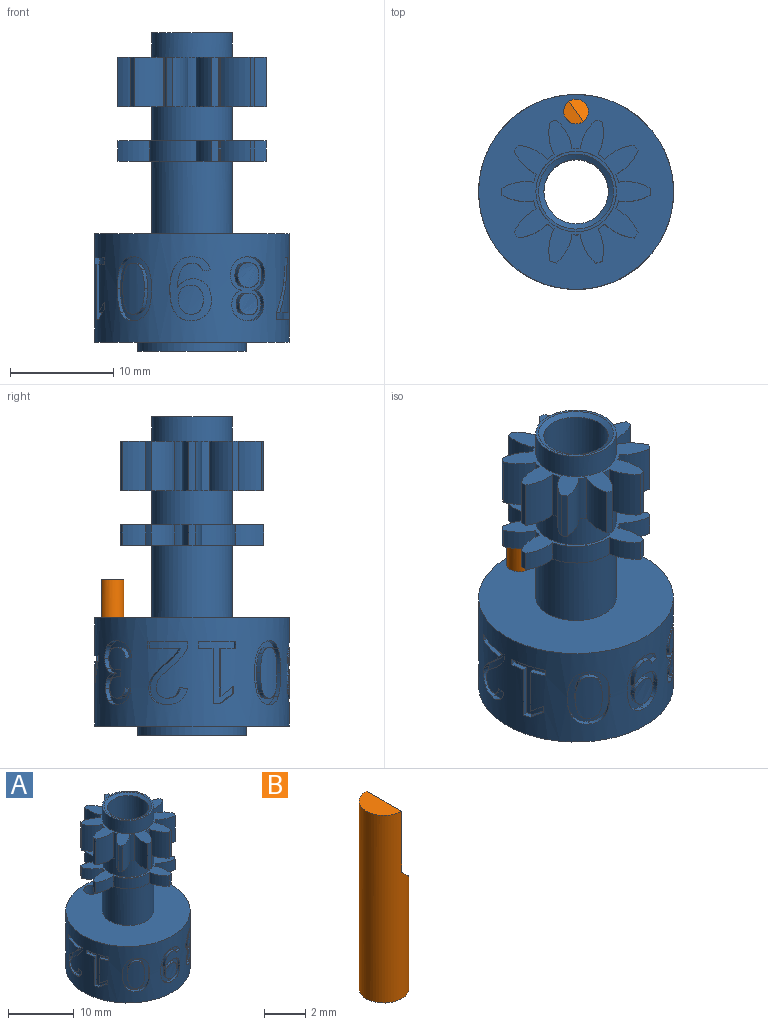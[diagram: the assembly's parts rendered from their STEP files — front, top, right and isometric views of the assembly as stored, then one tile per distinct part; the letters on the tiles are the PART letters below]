
ASSEMBLY  parts=2 mates=1
PART A: 322 faces, bbox 19.1x19x30.9 mm
  f0: cylinder r=9.45mm len=18.9mm, axis (0,0,-1), area 491.1mm2, adj f6,f7,f91,f92,f93,f94,f95,f102
  f1: cylinder r=3.9mm len=7.8mm, axis (0,0,-1), area 58.8mm2, adj f9,f87
  f2: cylinder r=3.9mm len=7.8mm, axis (0,0,-1), area 80.9mm2, adj f13,f88
  f3: cone r=3.12mm half-angle=30deg, axis (0,0,-1), area 49.7mm2, adj f4,f10
  f4: plane 10.5x10.5mm, normal (0,0,-1), area 31.2mm2, adj f3,f5
  f5: cylinder r=5.25mm len=10.5mm, axis (0,0,-1), area 29.7mm2, adj f4,f6
  f6: plane 18.9x18.9mm, normal (0,0,-1), area 189.4mm2, adj f0,f5,f11
  f7: plane 18.9x18.9mm, normal (0,0,1), area 228.2mm2, adj f0,f8,f11
  f8: cylinder r=3.9mm len=7.8mm, axis (0,0,-1), area 172.8mm2, adj f7,f14
  f9: plane 7.8x7.8mm, normal (0,0,1), area 6.2mm2, adj f1,f12
  f10: cylinder r=3.12mm len=28.73mm, axis (0,0,-1), area 563.2mm2, adj f3,f12
  f11: cylinder r=1.2mm len=10.5mm, axis (0,0,1), area 77.2mm2, adj f6,f7,f89,f90,f91,f92,f93,f94
  f12: cone r=3.64mm half-angle=60deg, axis (0,0,1), area 12.7mm2, adj f9,f10
  f13: plane 14.4x13.88mm, normal (0,0,1), area 46.7mm2, adj f2,f15,f16,f17,f18,f19,f20,f21
  f14: plane 14.4x13.88mm, normal (0,0,-1), area 46.7mm2, adj f8,f15,f16,f17,f18,f19,f20,f21
  f15: cylinder r=4.2mm len=1.95mm, axis (0,0,-1), area 1.6mm2, adj f13,f14,f16,f17
  f16: cylinder r=4.5mm len=2.3mm, axis (0,0,-1), area 6.3mm2, adj f13,f14,f15,f21
  f17: cylinder r=4.5mm len=3.09mm, axis (0,0,-1), area 6.3mm2, adj f13,f14,f15,f46
  f18: cylinder r=4.5mm len=2.85mm, axis (0,0,-1), area 6.3mm2, adj f13,f14,f19,f21
  f19: cylinder r=4.2mm len=1.95mm, axis (0,0,-1), area 1.6mm2, adj f13,f14,f18,f20
  f20: cylinder r=4.5mm len=3.12mm, axis (0,0,-1), area 6.3mm2, adj f13,f14,f19,f25
  f21: cylinder r=7.2mm len=1.95mm, axis (0,0,-1), area 1.2mm2, adj f13,f14,f16,f18
  f22: cylinder r=4.5mm len=2.76mm, axis (0,0,-1), area 6.3mm2, adj f13,f14,f23,f25
  f23: cylinder r=4.2mm len=1.95mm, axis (0,0,-1), area 1.6mm2, adj f13,f14,f22,f24
  f24: cylinder r=4.5mm len=2.76mm, axis (0,0,-1), area 6.3mm2, adj f13,f14,f23,f29
  f25: cylinder r=7.2mm len=1.95mm, axis (0,0,-1), area 1.2mm2, adj f13,f14,f20,f22
  f26: cylinder r=4.5mm len=3.12mm, axis (0,0,-1), area 6.3mm2, adj f13,f14,f27,f29
  f27: cylinder r=4.2mm len=1.95mm, axis (0,0,-1), area 1.6mm2, adj f13,f14,f26,f28
  f28: cylinder r=4.5mm len=2.85mm, axis (0,0,-1), area 6.3mm2, adj f13,f14,f27,f33
  f29: cylinder r=7.2mm len=1.95mm, axis (0,0,-1), area 1.2mm2, adj f13,f14,f24,f26
  f30: cylinder r=4.5mm len=2.3mm, axis (0,0,-1), area 6.3mm2, adj f13,f14,f31,f33
  f31: cylinder r=4.2mm len=1.95mm, axis (0,0,-1), area 1.6mm2, adj f13,f14,f30,f32
  f32: cylinder r=4.5mm len=3.09mm, axis (0,0,-1), area 6.3mm2, adj f13,f14,f31,f37
  f33: cylinder r=7.2mm len=1.95mm, axis (0,0,-1), area 1.2mm2, adj f13,f14,f28,f30
  f34: cylinder r=4.5mm len=3.09mm, axis (0,0,-1), area 6.3mm2, adj f13,f14,f35,f37
  f35: cylinder r=4.2mm len=1.95mm, axis (0,0,-1), area 1.6mm2, adj f13,f14,f34,f36
  f36: cylinder r=4.5mm len=2.3mm, axis (0,0,-1), area 6.3mm2, adj f13,f14,f35,f41
  f37: cylinder r=7.2mm len=1.95mm, axis (0,0,-1), area 1.2mm2, adj f13,f14,f32,f34
  f38: cylinder r=4.5mm len=2.85mm, axis (0,0,-1), area 6.3mm2, adj f13,f14,f39,f41
  f39: cylinder r=4.2mm len=1.95mm, axis (0,0,-1), area 1.6mm2, adj f13,f14,f38,f40
  f40: cylinder r=4.5mm len=3.12mm, axis (0,0,-1), area 6.3mm2, adj f13,f14,f39,f44
  f41: cylinder r=7.2mm len=1.95mm, axis (0,0,-1), area 1.2mm2, adj f13,f14,f36,f38
  f42: cylinder r=4.5mm len=2.76mm, axis (0,0,-1), area 6.3mm2, adj f13,f14,f43,f44
  f43: cylinder r=4.2mm len=4.5mm, axis (0,0,-1), area 11.9mm2, adj f13,f14,f42,f45
  f44: cylinder r=7.2mm len=1.95mm, axis (0,0,-1), area 1.2mm2, adj f13,f14,f40,f42
  f45: cylinder r=4.5mm len=3.09mm, axis (0,0,-1), area 6.3mm2, adj f13,f14,f43,f46
  f46: cylinder r=7.2mm len=1.95mm, axis (0,0,-1), area 1.2mm2, adj f13,f14,f17,f45
  f47: cylinder r=4.5mm len=4.8mm, axis (0,0,-1), area 15.4mm2, adj f48,f86,f87,f88
  f48: cylinder r=7.2mm len=4.8mm, axis (0,0,-1), area 3.1mm2, adj f47,f49,f87,f88
  f49: cylinder r=4.5mm len=4.8mm, axis (0,0,-1), area 15.4mm2, adj f48,f50,f87,f88
  f50: cylinder r=4.2mm len=4.8mm, axis (0,0,-1), area 3.9mm2, adj f49,f51,f87,f88
  f51: cylinder r=4.5mm len=4.8mm, axis (0,0,-1), area 15.4mm2, adj f50,f52,f87,f88
  f52: cylinder r=7.2mm len=4.8mm, axis (0,0,-1), area 3.1mm2, adj f51,f53,f87,f88
  f53: cylinder r=4.5mm len=4.8mm, axis (0,0,-1), area 15.4mm2, adj f52,f54,f87,f88
  f54: cylinder r=4.2mm len=4.8mm, axis (0,0,-1), area 3.9mm2, adj f53,f55,f87,f88
  f55: cylinder r=4.5mm len=4.8mm, axis (0,0,-1), area 15.4mm2, adj f54,f56,f87,f88
  f56: cylinder r=7.2mm len=4.8mm, axis (0,0,-1), area 3.1mm2, adj f55,f57,f87,f88
  f57: cylinder r=4.5mm len=4.8mm, axis (0,0,-1), area 15.4mm2, adj f56,f58,f87,f88
  f58: cylinder r=4.2mm len=4.8mm, axis (0,0,-1), area 3.9mm2, adj f57,f59,f87,f88
  f59: cylinder r=4.5mm len=4.8mm, axis (0,0,-1), area 15.4mm2, adj f58,f60,f87,f88
  f60: cylinder r=7.2mm len=4.8mm, axis (0,0,-1), area 3.1mm2, adj f59,f61,f87,f88
  f61: cylinder r=4.5mm len=4.8mm, axis (0,0,-1), area 15.4mm2, adj f60,f62,f87,f88
  f62: cylinder r=4.2mm len=4.8mm, axis (0,0,-1), area 3.9mm2, adj f61,f63,f87,f88
  f63: cylinder r=4.5mm len=4.8mm, axis (0,0,-1), area 15.4mm2, adj f62,f64,f87,f88
  f64: cylinder r=7.2mm len=4.8mm, axis (0,0,-1), area 3.1mm2, adj f63,f65,f87,f88
  f65: cylinder r=4.5mm len=4.8mm, axis (0,0,-1), area 15.4mm2, adj f64,f66,f87,f88
  f66: cylinder r=4.2mm len=4.8mm, axis (0,0,-1), area 3.9mm2, adj f65,f67,f87,f88
  f67: cylinder r=4.5mm len=4.8mm, axis (0,0,-1), area 15.4mm2, adj f66,f68,f87,f88
  f68: cylinder r=7.2mm len=4.8mm, axis (0,0,-1), area 3.1mm2, adj f67,f69,f87,f88
  f69: cylinder r=4.5mm len=4.8mm, axis (0,0,-1), area 15.4mm2, adj f68,f70,f87,f88
  f70: cylinder r=4.2mm len=4.8mm, axis (0,0,-1), area 3.9mm2, adj f69,f71,f87,f88
  f71: cylinder r=4.5mm len=4.8mm, axis (0,0,-1), area 15.4mm2, adj f70,f72,f87,f88
  f72: cylinder r=7.2mm len=4.8mm, axis (0,0,-1), area 3.1mm2, adj f71,f73,f87,f88
  f73: cylinder r=4.5mm len=4.8mm, axis (0,0,-1), area 15.4mm2, adj f72,f74,f87,f88
  f74: cylinder r=4.2mm len=4.8mm, axis (0,0,-1), area 3.9mm2, adj f73,f75,f87,f88
  f75: cylinder r=4.5mm len=4.8mm, axis (0,0,-1), area 15.4mm2, adj f74,f76,f87,f88
  f76: cylinder r=7.2mm len=4.8mm, axis (0,0,-1), area 3.1mm2, adj f75,f77,f87,f88
  f77: cylinder r=4.5mm len=4.8mm, axis (0,0,-1), area 15.4mm2, adj f76,f78,f87,f88
  f78: cylinder r=4.2mm len=4.8mm, axis (0,0,-1), area 3.9mm2, adj f77,f79,f87,f88
  f79: cylinder r=4.5mm len=4.8mm, axis (0,0,-1), area 15.4mm2, adj f78,f80,f87,f88
  f80: cylinder r=7.2mm len=4.8mm, axis (0,0,-1), area 3.1mm2, adj f79,f81,f87,f88
  f81: cylinder r=4.5mm len=4.8mm, axis (0,0,-1), area 15.4mm2, adj f80,f82,f87,f88
  f82: cylinder r=4.2mm len=4.8mm, axis (0,0,-1), area 3.9mm2, adj f81,f83,f87,f88
  f83: cylinder r=4.5mm len=4.8mm, axis (0,0,-1), area 15.4mm2, adj f82,f84,f87,f88
  f84: cylinder r=7.2mm len=4.8mm, axis (0,0,-1), area 3.1mm2, adj f83,f85,f87,f88
  f85: cylinder r=4.5mm len=4.8mm, axis (0,0,-1), area 15.4mm2, adj f84,f86,f87,f88
  f86: cylinder r=4.2mm len=4.8mm, axis (0,0,-1), area 3.9mm2, adj f47,f85,f87,f88
  f87: plane 14.4x13.88mm, normal (0,0,1), area 56.4mm2, adj f1,f47,f48,f49,f50,f51,f52,f53
  f88: plane 14.4x13.88mm, normal (0,0,-1), area 56.4mm2, adj f2,f47,f48,f49,f50,f51,f52,f53
  f89: cylinder r=8.95mm len=6.02mm, axis (0,0,-1), area 4mm2, adj f11,f91,f95,f102,f103,f104,f105,f106
  f90: cylinder r=8.95mm len=3.92mm, axis (0,0,-1), area 3.2mm2, adj f11,f93,f94,f96,f100,f101,f108,f109
  f91: plane 0.74x0.55mm, normal (0,0,-1), area 0.4mm2, adj f0,f11,f89,f92,f104
  f92: plane 1.36x0.47mm, normal (1,0.02,0), area 0.6mm2, adj f0,f11,f91,f93
  f93: plane 2.84x0.81mm, normal (0,0,-1), area 1.4mm2, adj f0,f11,f90,f92,f101,f107
  f94: plane 4.08x2.78mm, normal (0.83,0.02,0.56), area 2.4mm2, adj f0,f11,f90,f95,f101,f107
  f95: plane 0.82x0.55mm, normal (0,0,1), area 0.4mm2, adj f0,f11,f89,f94,f105
  f96: plane 2.28x1.56mm, normal (-0.83,-0.02,-0.56), area 1.4mm2, adj f11,f90,f97,f109,f167
  f97: extruded ~0.46x0.28mm, area 0.1mm2, adj f11,f96,f98,f167
  f98: extruded ~0.47x0.23mm, area 0.1mm2, adj f11,f97,f99,f167
  f99: plane 3.18x0.47mm, normal (1,0.02,0), area 1.5mm2, adj f11,f98,f100,f167
  f100: plane 2.13x0.71mm, normal (0,0,1), area 1mm2, adj f11,f90,f99,f108,f167
  f101: plane 1.05x0.31mm, normal (-0.02,1,0), area 0.3mm2, adj f90,f93,f94,f107
  f102: plane 0.61x0.51mm, normal (-1,-0.02,0), area 0.3mm2, adj f0,f89,f103,f106
  f103: plane 0.86x0.64mm, normal (0,0,-1), area 0.4mm2, adj f0,f89,f102,f104
  f104: plane 1.36x0.5mm, normal (-1,-0.02,0), area 0.7mm2, adj f0,f89,f91,f103
  f105: plane 4.05x0.5mm, normal (-1,-0.02,0), area 2mm2, adj f0,f89,f95,f106
  f106: plane 0.86x0.64mm, normal (0,0,1), area 0.4mm2, adj f0,f89,f102,f105
  f107: plane 0.6x0.44mm, normal (1,0.02,0), area 0.3mm2, adj f0,f93,f94,f101
  f108: plane 0.52x0.08mm, normal (-0.78,-0.02,-0.63), area 0.1mm2, adj f90,f100,f109,f167
  f109: plane 0.55x0.32mm, normal (-0.81,-0.02,-0.59), area 0.2mm2, adj f90,f96,f108,f167
  f110: cylinder r=8.95mm len=6.19mm, axis (0,0,-1), area 9.9mm2, adj f111,f112,f113,f114,f115,f116,f117,f118
  f111: plane 0.39x0.31mm, normal (-0.78,-0.62,0), area 0mm2, adj f0,f110,f112,f139
  f112: extruded ~1.11x1.06mm, area 0.5mm2, adj f0,f110,f111,f113
  f113: extruded ~0.94x0.64mm, area 0.5mm2, adj f0,f110,f112,f114
  f114: extruded ~1.17x0.78mm, area 0.7mm2, adj f0,f110,f113,f115
  f115: extruded ~1.47x1.34mm, area 0.8mm2, adj f0,f110,f114,f116
  f116: extruded ~1.45x1.33mm, area 0.7mm2, adj f0,f110,f115,f117
  f117: extruded ~1.15x0.87mm, area 0.7mm2, adj f0,f110,f116,f118,f141
  f118: plane 0.99x0.83mm, normal (0.06,0.05,-1), area 0.4mm2, adj f0,f110,f117,f119,f141
  f119: extruded ~0.73x0.66mm, area 0.4mm2, adj f0,f110,f118,f120
  f120: extruded ~0.99x0.94mm, area 0.4mm2, adj f0,f110,f119,f121
  f121: extruded ~0.99x0.94mm, area 0.5mm2, adj f0,f110,f120,f122
  f122: extruded ~0.76x0.59mm, area 0.4mm2, adj f0,f110,f121,f123
  f123: extruded ~0.76x0.63mm, area 0.4mm2, adj f0,f110,f122,f124
  f124: extruded ~1.09x1.01mm, area 0.5mm2, adj f0,f110,f123,f125
  f125: plane 0.67x0.62mm, normal (0,0,1), area 0.2mm2, adj f0,f110,f124,f126
  f126: plane 0.67x0.39mm, normal (0.78,0.62,0), area 0.3mm2, adj f0,f110,f125,f127
  f127: plane 0.68x0.64mm, normal (0,0,-1), area 0.2mm2, adj f0,f110,f126,f128
  f128: extruded ~1.18x1.09mm, area 0.6mm2, adj f0,f110,f127,f129
  f129: extruded ~0.77x0.66mm, area 0.4mm2, adj f0,f110,f128,f130
  f130: extruded ~0.85x0.63mm, area 0.5mm2, adj f0,f110,f129,f131
  f131: extruded ~1.05x0.99mm, area 0.5mm2, adj f0,f110,f130,f132
  f132: extruded ~1.41x1.29mm, area 0.9mm2, adj f0,f110,f131,f133
  f133: plane 1x0.84mm, normal (0.07,0.06,1), area 0.4mm2, adj f0,f110,f132,f134,f140
  f134: extruded ~1.22x0.89mm, area 0.7mm2, adj f0,f110,f133,f135,f140
  f135: extruded ~1.54x1.4mm, area 0.8mm2, adj f0,f110,f134,f136
  f136: extruded ~1.57x1.42mm, area 0.8mm2, adj f0,f110,f135,f137
  f137: extruded ~1.29x0.8mm, area 0.7mm2, adj f0,f110,f136,f138
  f138: extruded ~0.96x0.69mm, area 0.5mm2, adj f0,f110,f137,f139
  f139: extruded ~1.21x1.14mm, area 0.6mm2, adj f0,f110,f111,f138
  f140: plane 0.49x0.09mm, normal (-0.62,0.78,0), area 0mm2, adj f110,f133,f134
  f141: plane 0.06x0.01mm, normal (-0.62,0.78,0), area 0mm2, adj f110,f117,f118
  f142: cylinder r=8.95mm len=6.11mm, axis (0,0,-1), area 8.9mm2, adj f143,f144,f145,f146,f147,f148,f149,f150
  f143: plane 3.13x1.43mm, normal (0,0,1), area 1.6mm2, adj f0,f142,f144,f166
  f144: extruded ~0.64x0.62mm, area 0.4mm2, adj f0,f142,f143,f145
  f145: extruded ~0.9x0.72mm, area 0.5mm2, adj f0,f142,f144,f146
  f146: extruded ~1.32x1.07mm, area 0.8mm2, adj f0,f142,f145,f147
  f147: extruded ~0.69x0.69mm, area 0.4mm2, adj f0,f142,f146,f148
  f148: extruded ~0.7x0.56mm, area 0.4mm2, adj f0,f142,f147,f149
  f149: extruded ~1.22x0.7mm, area 0.7mm2, adj f0,f142,f148,f150
  f150: extruded ~1.51x0.95mm, area 0.8mm2, adj f0,f142,f149,f151
  f151: extruded ~1.47x0.95mm, area 0.7mm2, adj f0,f142,f150,f152
  f152: extruded ~1.15x0.77mm, area 0.7mm2, adj f0,f142,f151,f153
  f153: plane 0.93x0.56mm, normal (0.02,0.09,-1), area 0.4mm2, adj f0,f142,f152,f154
  f154: extruded ~0.75x0.63mm, area 0.4mm2, adj f0,f142,f153,f155
  f155: extruded ~0.92x0.74mm, area 0.4mm2, adj f0,f142,f154,f156
  f156: extruded ~0.92x0.72mm, area 0.4mm2, adj f0,f142,f155,f157
  f157: extruded ~0.77x0.59mm, area 0.4mm2, adj f0,f142,f156,f158
  f158: extruded ~0.66x0.55mm, area 0.3mm2, adj f0,f142,f157,f159
  f159: extruded ~0.63x0.57mm, area 0.4mm2, adj f0,f142,f158,f160
  f160: extruded ~0.73x0.65mm, area 0.4mm2, adj f0,f142,f159,f161
  f161: extruded ~0.8x0.7mm, area 0.4mm2, adj f0,f142,f160,f162
  f162: extruded ~0.79x0.75mm, area 0.5mm2, adj f0,f142,f161,f163
  f163: extruded ~0.88x0.74mm, area 0.5mm2, adj f0,f142,f162,f164
  f164: plane 0.54x0.5mm, normal (0.26,0.96,0), area 0.3mm2, adj f0,f142,f163,f165
  f165: plane 3.99x1.51mm, normal (0,0,-1), area 2mm2, adj f0,f142,f164,f166
  f166: plane 0.65x0.49mm, normal (-0.26,-0.96,0), area 0.3mm2, adj f0,f142,f143,f165
  f167: cylinder r=9.45mm len=3.18mm, axis (0,0,-1), area 3.3mm2, adj f96,f97,f98,f99,f100,f108,f109
  f168: cylinder r=8.95mm len=6.1mm, axis (0,0,-1), area 9.8mm2, adj f169,f170,f171,f172,f173,f174,f175,f176
  f169: extruded ~1.35x1.2mm, area 0.7mm2, adj f0,f168,f170,f189
  f170: plane 1.91x0.47mm, normal (-0.81,0.58,-0.06), area 1mm2, adj f0,f168,f169,f171
  f171: plane 2.46x2.05mm, normal (0,0,-1), area 1.4mm2, adj f0,f168,f170,f172
  f172: plane 0.65x0.41mm, normal (-0.81,0.58,0), area 0.3mm2, adj f0,f168,f171,f173
  f173: plane 3.1x2.37mm, normal (0,0,1), area 1.7mm2, adj f0,f168,f172,f174
  f174: plane 3.24x0.5mm, normal (0.81,-0.58,0.06), area 1.7mm2, adj f0,f168,f173,f175
  f175: plane 0.99x0.74mm, normal (0,0,-1), area 0.4mm2, adj f0,f168,f174,f176
  f176: extruded ~0.77x0.77mm, area 0.3mm2, adj f0,f168,f175,f177
  f177: extruded ~0.78x0.77mm, area 0.3mm2, adj f0,f168,f176,f178
  f178: extruded ~1.08x0.99mm, area 0.5mm2, adj f0,f168,f177,f179
  f179: extruded ~0.92x0.64mm, area 0.5mm2, adj f0,f168,f178,f180
  f180: extruded ~1.03x0.64mm, area 0.6mm2, adj f0,f168,f179,f181
  f181: extruded ~1.1x1mm, area 0.5mm2, adj f0,f168,f180,f182
  f182: extruded ~1.37x1.23mm, area 0.8mm2, adj f0,f168,f181,f183
  f183: plane 1.01x0.74mm, normal (0.09,-0.07,0.99), area 0.4mm2, adj f0,f168,f182,f184,f190
  f184: extruded ~1.06x0.89mm, area 0.7mm2, adj f0,f168,f183,f185,f190
  f185: extruded ~1.47x1.31mm, area 0.7mm2, adj f0,f168,f184,f186
  f186: extruded ~1.63x1.41mm, area 0.9mm2, adj f0,f168,f185,f187
  f187: extruded ~1.5x0.83mm, area 0.8mm2, adj f0,f168,f186,f188
  f188: extruded ~1.36x0.8mm, area 0.8mm2, adj f0,f168,f187,f189
  f189: extruded ~1.51x1.32mm, area 0.8mm2, adj f0,f168,f169,f188
  f190: plane 0.37x0.09mm, normal (0.58,0.81,0), area 0mm2, adj f168,f183,f184
  f191: cylinder r=8.95mm len=6.19mm, axis (0,0,-1), area 10.3mm2, adj f192,f193,f194,f195,f196,f197,f198,f199
  f192: extruded ~1.45x0.99mm, area 0.7mm2, adj f0,f191,f193,f206
  f193: extruded ~1.4x0.72mm, area 0.8mm2, adj f0,f191,f192,f194
  f194: extruded ~1.5x0.73mm, area 0.8mm2, adj f0,f191,f193,f195
  f195: extruded ~1.55x1.02mm, area 0.8mm2, adj f0,f191,f194,f196
  f196: extruded ~1.67x1.08mm, area 0.9mm2, adj f0,f191,f195,f197
  f197: extruded ~2.2x0.75mm, area 1.2mm2, adj f0,f191,f196,f198
  f198: extruded ~2.4x0.76mm, area 1.3mm2, adj f0,f191,f197,f199
  f199: extruded ~1.71x1.09mm, area 0.9mm2, adj f0,f191,f198,f200
  f200: extruded ~1.84x1.23mm, area 1.2mm2, adj f0,f191,f199,f201
  f201: plane 0.89x0.6mm, normal (-0.05,0.17,-0.98), area 0.4mm2, adj f0,f191,f200,f202
  f202: extruded ~1.11x0.84mm, area 0.7mm2, adj f0,f191,f201,f203
  f203: extruded ~1.14x0.84mm, area 0.6mm2, adj f0,f191,f202,f204
  f204: extruded ~1.77x0.63mm, area 0.9mm2, adj f0,f191,f203,f205
  f205: extruded ~0.74x0.72mm, area 0.4mm2, adj f0,f191,f204,f206
  f206: extruded ~0.99x0.77mm, area 0.5mm2, adj f0,f191,f192,f205
  f207: extruded ~1.01x0.79mm, area 0.5mm2, adj f191,f208,f214,f318
  f208: extruded ~1.14x0.62mm, area 0.6mm2, adj f191,f207,f209,f318
  f209: extruded ~0.87x0.62mm, area 0.5mm2, adj f191,f208,f210,f318
  f210: extruded ~1x0.79mm, area 0.5mm2, adj f191,f209,f211,f318
  f211: extruded ~1.01x0.79mm, area 0.5mm2, adj f191,f210,f212,f318
  f212: extruded ~1.01x0.61mm, area 0.5mm2, adj f191,f211,f213,f318
  f213: extruded ~1.03x0.61mm, area 0.6mm2, adj f191,f212,f214,f318
  f214: extruded ~0.99x0.78mm, area 0.5mm2, adj f191,f207,f213,f318
  f215: cylinder r=8.95mm len=6.02mm, axis (0,0,-1), area 6.5mm2, adj f216,f217,f218,f219,f220,f221,f222,f223
  f216: plane 0.65x0.49mm, normal (-0.32,-0.95,0), area 0.3mm2, adj f0,f215,f217,f225
  f217: plane 3.28x1.36mm, normal (0,0,-1), area 1.6mm2, adj f0,f215,f216,f218
  f218: extruded ~2.94x1.73mm, area 1.7mm2, adj f0,f215,f217,f219
  f219: extruded ~2.43x0.67mm, area 1.2mm2, adj f0,f215,f218,f220
  f220: plane 0.94x0.69mm, normal (0,0,-1), area 0.4mm2, adj f0,f215,f219,f221
  f221: extruded ~1.61x0.54mm, area 0.8mm2, adj f0,f215,f220,f222
  f222: extruded ~1.58x0.71mm, area 0.8mm2, adj f0,f215,f221,f223
  f223: extruded ~2.21x1.45mm, area 1.3mm2, adj f0,f215,f222,f224
  f224: plane 0.62x0.48mm, normal (0.32,0.95,0), area 0.3mm2, adj f0,f215,f223,f225
  f225: plane 3.94x1.72mm, normal (0,0,1), area 2mm2, adj f0,f215,f216,f224
  f226: cylinder r=8.95mm len=6.19mm, axis (0,0,-1), area 11.8mm2, adj f227,f228,f229,f230,f231,f232,f233,f234
  f227: plane 1.03x0.06mm, normal (0.57,-0.82,0), area 0mm2, adj f226,f233,f234
  f228: extruded ~1.09x1.02mm, area 0.5mm2, adj f0,f226,f229,f245
  f229: extruded ~0.99x0.65mm, area 0.5mm2, adj f0,f226,f228,f230
  f230: extruded ~1.3x0.8mm, area 0.7mm2, adj f0,f226,f229,f231
  f231: extruded ~1.6x1.37mm, area 0.8mm2, adj f0,f226,f230,f232
  f232: extruded ~1.61x1.4mm, area 0.8mm2, adj f0,f226,f231,f233
  f233: extruded ~1.3x0.81mm, area 0.8mm2, adj f0,f226,f227,f232,f234
  f234: extruded ~0.99x0.66mm, area 0.6mm2, adj f0,f226,f227,f233,f235
  f235: extruded ~1.07x1.02mm, area 0.5mm2, adj f0,f226,f234,f236
  f236: plane 0.41x0.29mm, normal (-0.82,-0.57,0), area 0mm2, adj f0,f226,f235,f237
  f237: extruded ~0.99x0.95mm, area 0.5mm2, adj f0,f226,f236,f238
  f238: extruded ~0.9x0.63mm, area 0.5mm2, adj f0,f226,f237,f239
  f239: extruded ~1.11x0.8mm, area 0.6mm2, adj f0,f226,f238,f240
  f240: extruded ~1.49x1.31mm, area 0.7mm2, adj f0,f226,f239,f241
  f241: extruded ~1.49x1.29mm, area 0.8mm2, adj f0,f226,f240,f242
  f242: extruded ~1.13x0.78mm, area 0.7mm2, adj f0,f226,f241,f243
  f243: extruded ~0.9x0.62mm, area 0.5mm2, adj f0,f226,f242,f244
  f244: extruded ~0.98x0.94mm, area 0.5mm2, adj f0,f226,f243,f245
  f245: plane 0.41x0.29mm, normal (0.82,0.57,0), area 0mm2, adj f0,f226,f228,f244
  f246: extruded ~0.98x0.91mm, area 0.4mm2, adj f226,f247,f252,f260
  f247: extruded ~0.81x0.6mm, area 0.4mm2, adj f226,f246,f248,f260
  f248: extruded ~1.24x1.1mm, area 0.9mm2, adj f226,f247,f249,f260
  f249: extruded ~0.99x0.92mm, area 0.4mm2, adj f226,f248,f250,f260
  f250: extruded ~0.76x0.6mm, area 0.4mm2, adj f226,f249,f251,f260
  f251: extruded ~0.79x0.61mm, area 0.4mm2, adj f226,f250,f252,f260
  f252: extruded ~0.99x0.92mm, area 0.4mm2, adj f226,f246,f251,f260
  f253: extruded ~1.39x1.24mm, area 1mm2, adj f226,f254,f259,f319
  f254: extruded ~0.84x0.64mm, area 0.5mm2, adj f226,f253,f255,f319
  f255: extruded ~1.07x0.98mm, area 0.5mm2, adj f226,f254,f256,f319
  f256: extruded ~1.07x0.97mm, area 0.5mm2, adj f226,f255,f257,f319
  f257: extruded ~0.84x0.63mm, area 0.5mm2, adj f226,f256,f258,f319
  f258: extruded ~0.96x0.62mm, area 0.5mm2, adj f226,f257,f259,f319
  f259: extruded ~1.07x0.98mm, area 0.5mm2, adj f226,f253,f258,f319
  f260: cylinder r=9.45mm len=2.08mm, axis (0,0,-1), area 3.2mm2, adj f246,f247,f248,f249,f250,f251,f252
  f261: cylinder r=8.95mm len=6.19mm, axis (0,0,-1), area 10.5mm2, adj f262,f263,f264,f265,f266,f267,f268,f269
  f262: plane 0.67x0.02mm, normal (-0.03,-1,0), area 0mm2, adj f261,f276,f277
  f263: extruded ~1.54x0.74mm, area 0.9mm2, adj f0,f261,f264,f278
  f264: extruded ~2.23x0.62mm, area 1.2mm2, adj f0,f261,f263,f265
  f265: extruded ~2.38x0.63mm, area 1.3mm2, adj f0,f261,f264,f266
  f266: extruded ~1.63x0.83mm, area 1mm2, adj f0,f261,f265,f267
  f267: extruded ~1.15x0.63mm, area 0.6mm2, adj f0,f261,f266,f268
  f268: extruded ~0.96x0.64mm, area 0.6mm2, adj f0,f261,f267,f269
  f269: plane 0.75x0.62mm, normal (-0.16,0,0.99), area 0.4mm2, adj f0,f261,f268,f270
  f270: extruded ~1.03x0.75mm, area 0.7mm2, adj f0,f261,f269,f271
  f271: extruded ~1.04x0.62mm, area 0.6mm2, adj f0,f261,f270,f272
  f272: extruded ~1.75x0.55mm, area 0.9mm2, adj f0,f261,f271,f273
  f273: extruded ~0.62x0.6mm, area 0.4mm2, adj f0,f261,f272,f274
  f274: extruded ~0.92x0.54mm, area 0.5mm2, adj f0,f261,f273,f275
  f275: extruded ~1.31x0.68mm, area 0.7mm2, adj f0,f261,f274,f276
  f276: extruded ~1.47x0.62mm, area 0.8mm2, adj f0,f261,f262,f275,f277
  f277: extruded ~1.48x0.63mm, area 0.8mm2, adj f0,f261,f262,f276,f278
  f278: extruded ~1.49x0.68mm, area 0.8mm2, adj f0,f261,f263,f277
  f279: extruded ~0.63x0.53mm, area 0.3mm2, adj f261,f280,f287,f320
  f280: extruded ~0.88x0.58mm, area 0.5mm2, adj f261,f279,f281,f320
  f281: extruded ~1.04x0.55mm, area 0.6mm2, adj f261,f280,f282,f320
  f282: extruded ~1.02x0.55mm, area 0.6mm2, adj f261,f281,f283,f320
  f283: extruded ~0.89x0.58mm, area 0.5mm2, adj f261,f282,f284,f320
  f284: extruded ~0.91x0.55mm, area 0.5mm2, adj f261,f283,f285,f320
  f285: extruded ~1.17x0.55mm, area 0.6mm2, adj f261,f284,f286,f320
  f286: extruded ~0.63x0.53mm, area 0.3mm2, adj f261,f285,f287,f320
  f287: extruded ~0.55x0.47mm, area 0.3mm2, adj f261,f279,f286,f320
  f288: cylinder r=8.95mm len=6.19mm, axis (0,0,-1), area 9.9mm2, adj f289,f290,f291,f292,f293,f294,f295,f296
  f289: plane 2.68x0.12mm, normal (-0.62,-0.79,0), area 0.2mm2, adj f288,f295,f296
  f290: extruded ~1.62x1.46mm, area 0.9mm2, adj f0,f288,f291,f297
  f291: extruded ~2.32x0.79mm, area 1.2mm2, adj f0,f288,f290,f292
  f292: extruded ~2.3x0.81mm, area 1.2mm2, adj f0,f288,f291,f293
  f293: extruded ~1.61x1.45mm, area 0.9mm2, adj f0,f288,f292,f294
  f294: extruded ~1.63x1.48mm, area 0.9mm2, adj f0,f288,f293,f295
  f295: extruded ~2.31x0.79mm, area 1.2mm2, adj f0,f288,f289,f294,f296
  f296: extruded ~2.32x0.78mm, area 1.2mm2, adj f0,f288,f289,f295,f297
  f297: extruded ~1.67x1.51mm, area 0.9mm2, adj f0,f288,f290,f296
  f298: extruded ~1.14x1.06mm, area 0.6mm2, adj f288,f299,f305,f321
  f299: extruded ~1.87x0.63mm, area 1mm2, adj f288,f298,f300,f321
  f300: extruded ~1.9x0.62mm, area 1mm2, adj f288,f299,f301,f321
  f301: extruded ~1.15x1.08mm, area 0.6mm2, adj f288,f300,f302,f321
  f302: extruded ~1.12x1.04mm, area 0.6mm2, adj f288,f301,f303,f321
  f303: extruded ~1.89x0.61mm, area 1mm2, adj f288,f302,f304,f321
  f304: extruded ~1.86x0.62mm, area 1mm2, adj f288,f303,f305,f321
  f305: extruded ~1.12x1.04mm, area 0.6mm2, adj f288,f298,f304,f321
  f306: cylinder r=8.95mm len=6.02mm, axis (0,0,-1), area 7.6mm2, adj f307,f308,f309,f310,f311,f312,f313,f314
  f307: plane 1.6x0.69mm, normal (0,0,1), area 0.7mm2, adj f0,f306,f308,f317
  f308: plane 5.36x0.48mm, normal (0.26,-0.96,0), area 2.7mm2, adj f0,f306,f307,f309
  f309: plane 0.82x0.66mm, normal (0,0,1), area 0.4mm2, adj f0,f306,f308,f310
  f310: plane 1.47x1.01mm, normal (-0.15,0.55,0.82), area 0.9mm2, adj f0,f306,f309,f311
  f311: plane 0.73x0.49mm, normal (-0.26,0.96,0), area 0.4mm2, adj f0,f306,f310,f312
  f312: plane 1.41x0.99mm, normal (0.15,-0.56,-0.81), area 0.8mm2, adj f0,f306,f311,f313
  f313: plane 4.63x0.48mm, normal (-0.26,0.96,0), area 2.3mm2, adj f0,f306,f312,f314
  f314: plane 1.56x1.07mm, normal (0,0,1), area 0.8mm2, adj f0,f306,f313,f315
  f315: plane 0.65x0.49mm, normal (-0.26,0.96,0), area 0.3mm2, adj f0,f306,f314,f316
  f316: plane 3.78x1.47mm, normal (0,0,-1), area 1.9mm2, adj f0,f306,f315,f317
  f317: plane 0.65x0.49mm, normal (0.26,-0.96,0), area 0.3mm2, adj f0,f306,f307,f316
  f318: cylinder r=9.45mm len=2.76mm, axis (0,0,-1), area 4.9mm2, adj f207,f208,f209,f210,f211,f212,f213,f214
  f319: cylinder r=9.45mm len=2.39mm, axis (0,0,-1), area 4.1mm2, adj f253,f254,f255,f256,f257,f258,f259
  f320: cylinder r=9.45mm len=2.82mm, axis (0,0,-1), area 5mm2, adj f279,f280,f281,f282,f283,f284,f285,f286
  f321: cylinder r=9.45mm len=4.94mm, axis (0,0,-1), area 9.9mm2, adj f298,f299,f300,f301,f302,f303,f304,f305
PART B: 5 faces, bbox 2.4x2.4x11.1 mm
  f0: cylinder r=1.2mm len=11.1mm, axis (0,0,-1), area 67.2mm2, adj f1,f2,f3,f4
  f1: plane 2.4x1.2mm, normal (0,0,1), area 2.3mm2, adj f0,f3
  f2: plane 2.4x2.4mm, normal (0,0,-1), area 4.5mm2, adj f0
  f3: plane 3.6x2.4mm, normal (1,0,0), area 8.6mm2, adj f0,f1,f4
  f4: plane 2.4x1.2mm, normal (0.71,0,0.71), area 3.2mm2, adj f0,f3
PLACE A at identity fixed
PLACE B rot(axis=(0,0,1),36deg) t=(0,7.8,4)mm
MATE fastened B.f0 <-> A.f11  axis (0,0,-1) through (0,7.8,12.3)mm
